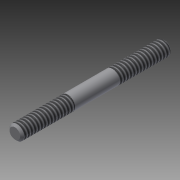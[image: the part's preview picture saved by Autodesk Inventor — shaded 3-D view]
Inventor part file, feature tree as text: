
AUTODESK INVENTOR PART (.ipt)
format: ipt  version: 2014 SP2 (Build 180246200, 246)  size: 96,768 bytes
history: native  units: in
note: dims shown in document units (in); Inventor stores cm internally (conversion verified against a paired STEP export)
features: other x7, thread x2, revolve x1, sketch x1
ambient origin geometry x8: Origin, YZ Plane, XZ Plane, XY Plane, X Axis, Y Axis, Z Axis, Center Point
bodies: Solid1 (feature_tree)
feature tree (11):
  revolve  "Revolution1"  [1 undecoded]
  thread  "Thread1"  [1 undecoded]
  thread  "Thread2"  [1 undecoded]
  other  "screw_XY"
  other  "screw_YZ"
  other  "screw_ZX"
  other  "screw_X"
  other  "screw_Y"
  other  "screw_Z"
  other  "screw_Center"
  sketch  "Sketch_3"  dims[d0=360.0deg d1=0.4814in d2=0.0in d3=0.4814in d4=0.0in]
note: 3 required parameter values undecoded (feature->parameter linkage not recoverable at this tier; creation-order binding heuristic only, values carry confidence <= 0.55)